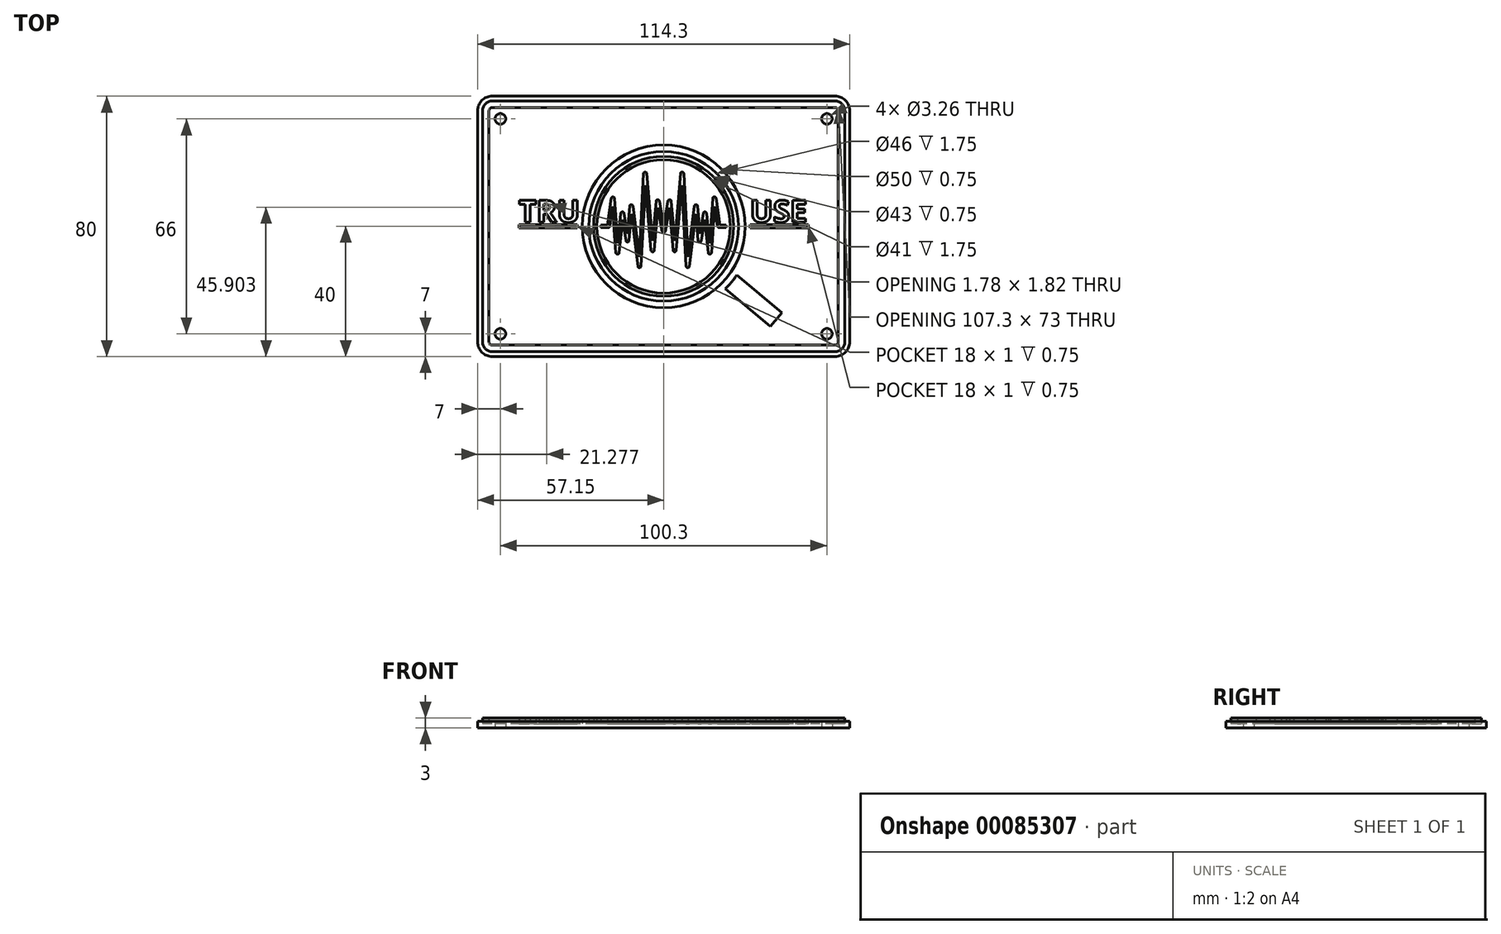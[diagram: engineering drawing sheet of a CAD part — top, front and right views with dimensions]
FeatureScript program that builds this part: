
annotation { "Feature Type Name" : "Feature", "Feature Type Description" : "" }
export const myFeature = defineFeature(function(context is Context, id is Id, definition is map)
    precondition{}
    {
        {
            var Q0;
            Q0=qCreatedBy(makeId("Front.planeOp"),FACE);
            var sketch = newSketch(context, id + "F0", { "sketchPlane" : qUnion([Q0])});
            skLineSegment(sketch, "E0.bottom", {"start": v(-57.15, 0) * mm, "end": v(57.15, 0) * mm});
            skLineSegment(sketch, "E0.top", {"start": v(-57.15, 2) * mm, "end": v(57.15, 2) * mm});
            skLineSegment(sketch, "E0.left", {"start": v(-57.15, 0) * mm, "end": v(-57.15, 2) * mm});
            skLineSegment(sketch, "E0.right", {"start": v(57.15, 0) * mm, "end": v(57.15, 2) * mm});
            skSolve(sketch);
        }
        {
            var Q0;
            Q0=makeQuery(id+"F0.imprint","IMPRINT",FACE,{"disambiguationData":[TD([[makeQuery(id+"F0.imprint","IMPRINT",EDGE,{"derivedFrom":sQuery(id+"F0.wireOp",EDGE,"E0.bottom")}),1.0]])]});
            extrude(context, id + "F1", {"entities" : qUnion([Q0]), "endBound" : BoundingType.SYMMETRIC, "depth" : 80 * mm});
        }
        {
            var Q0;
            Q0=qCreatedBy(makeId("Top.planeOp"),FACE);
            cPlane(context, id + "F2", {"entities" : qUnion([Q0]), "cplaneType" : CPlaneType.OFFSET, "offset" : 1.25 * mm, "width" : 150 * mm, "height" : 150 * mm});
        }
        {
            var Q0;
            Q0=qCreatedBy(id+"F2.planeOp",FACE);
            var sketch = newSketch(context, id + "F3", { "sketchPlane" : qUnion([Q0])});
            skCircle(sketch, "E1", {"center": v(0, 0) * mm, "radius": 25 * mm});
            skLineSegment(sketch, "E2.bottom", {"start": v(-44.5, -0.5) * mm, "end": v(-26.5, -0.5) * mm});
            skLineSegment(sketch, "E2.top", {"start": v(-44.5, 0.5) * mm, "end": v(-26.5, 0.5) * mm});
            skLineSegment(sketch, "E2.left", {"start": v(-44.5, -0.5) * mm, "end": v(-44.5, 0.5) * mm});
            skLineSegment(sketch, "E2.right", {"start": v(-26.5, -0.5) * mm, "end": v(-26.5, 0.5) * mm});
            skPoint(sketch, "E2.middle", {"position": v(-35.5, 0) * mm});
            skLineSegment(sketch, "E3.MirrorCS", {"start": v(44.5, 0.5) * mm, "end": v(26.5, 0.5) * mm});
            skLineSegment(sketch, "E4.MirrorCS", {"start": v(44.5, -0.5) * mm, "end": v(26.5, -0.5) * mm});
            skLineSegment(sketch, "E5.MirrorCS", {"start": v(26.5, -0.5) * mm, "end": v(26.5, 0.5) * mm});
            skLineSegment(sketch, "E6.MirrorCS", {"start": v(44.5, -0.5) * mm, "end": v(44.5, 0.5) * mm});
            skCircle(sketch, "E7", {"center": v(0, 0) * mm, "radius": 23 * mm});
            skSolve(sketch);
        }
        {
            var Q0;
            Q0 = qSketchRegion(id + "F3", true);
            extrude(context, id + "F4", {"entities" : qUnion([Q0]), "depth" : 1.75 * mm});
        }
        {
            var Q0;
            Q0=qCreatedBy(id+"F2.planeOp",FACE);
            var sketch = newSketch(context, id + "F5", { "sketchPlane" : qUnion([Q0])});
            skCircle(sketch, "E8", {"center": v(0, 0) * mm, "radius": 21.5 * mm});
            skCircle(sketch, "E9", {"center": v(0, 0) * mm, "radius": 20.5 * mm});
            skSolve(sketch);
        }
        {
            var Q0;
            Q0 = qSketchRegion(id + "F5", true);
            extrude(context, id + "F6", {"entities" : qUnion([Q0]), "depth" : 1.75 * mm});
        }
        {
            var Q0;
            Q0=qCreatedBy(id+"F2.planeOp",FACE);
            var sketch = newSketch(context, id + "F7", { "sketchPlane" : qUnion([Q0])});
            skLineSegment(sketch, "E10.0", {"start": v(19, -19.19) * mm, "end": v(32.78, -30.76) * mm});
            skLineSegment(sketch, "E11.0", {"start": v(22.49, -14.94) * mm, "end": v(36.32, -26.55) * mm});
            skLineSegment(sketch, "E12", {"start": v(36.32, -26.55) * mm, "end": v(32.78, -30.76) * mm});
            skArc(sketch, "E13", {"start": v(19, -19.19) * mm, "mid": v(20.85, -17.15) * mm, "end": v(22.49, -14.94) * mm});
            skSolve(sketch);
        }
        {
            var Q0;
            Q0 = qSketchRegion(id + "F7", true);
            extrude(context, id + "F8", {"entities" : qUnion([Q0]), "depth" : 1.75 * mm});
        }
        {
            var Q0;
            Q0=qCreatedBy(id+"F2.planeOp",FACE);
            var sketch = newSketch(context, id + "F9", { "sketchPlane" : qUnion([Q0])});
            skText(sketch, "E14", { "text": "TRU", "fontName": "OpenSans-Bold.ttf"});
            skText(sketch, "E15", { "text": "USE", "fontName": "OpenSans-Bold.ttf"});
            const initialGuessF9  = {"E14": [-0.0445, 0.00125, 1, 0, 0.00679], "E15": [0.0265, 0.00125, 1, 0, 0.00678]};
            skSetInitialGuess(sketch, initialGuessF9);
            skSolve(sketch);
        }
        {
            var Q0;
            Q0 = qSketchRegion(id + "F9", true);
            extrude(context, id + "F10", {"entities" : qUnion([Q0]), "depth" : 1.75 * mm});
        }
        {
            var Q0;
            Q0=qCreatedBy(id+"F2.planeOp",FACE);
            var sketch = newSketch(context, id + "F11", { "sketchPlane" : qUnion([Q0])});
            skPoint(sketch, "E16.middle", {"position": v(0, 0) * mm});
            skLineSegment(sketch, "E17.bottom", {"start": v(52.65, 38.5) * mm, "end": v(-52.65, 38.5) * mm});
            skLineSegment(sketch, "E17.top", {"start": v(52.65, -38.5) * mm, "end": v(-52.65, -38.5) * mm});
            skLineSegment(sketch, "E17.left", {"start": v(55.65, 35.5) * mm, "end": v(55.65, -35.5) * mm});
            skLineSegment(sketch, "E17.right", {"start": v(-55.65, 35.5) * mm, "end": v(-55.65, -35.5) * mm});
            skLineSegment(sketch, "E18.bottom", {"start": v(52.65, 36.5) * mm, "end": v(-52.65, 36.5) * mm});
            skLineSegment(sketch, "E18.top", {"start": v(52.65, -36.5) * mm, "end": v(-52.65, -36.5) * mm});
            skLineSegment(sketch, "E18.left", {"start": v(53.65, 35.5) * mm, "end": v(53.65, -35.5) * mm});
            skLineSegment(sketch, "E18.right", {"start": v(-53.65, 35.5) * mm, "end": v(-53.65, -35.5) * mm});
            skPoint(sketch, "E19.visualSharp", {"position": v(-55.65, 38.5) * mm});
            skArc(sketch, "E19.filletArc", {"start": v(-52.65, 38.5) * mm, "mid": v(-54.77, 37.62) * mm, "end": v(-55.65, 35.5) * mm});
            skPoint(sketch, "E20.visualSharp", {"position": v(55.65, 38.5) * mm});
            skArc(sketch, "E20.filletArc", {"start": v(55.65, 35.5) * mm, "mid": v(54.77, 37.62) * mm, "end": v(52.65, 38.5) * mm});
            skPoint(sketch, "E21.visualSharp", {"position": v(55.65, -38.5) * mm});
            skArc(sketch, "E21.filletArc", {"start": v(52.65, -38.5) * mm, "mid": v(54.77, -37.62) * mm, "end": v(55.65, -35.5) * mm});
            skPoint(sketch, "E22.visualSharp", {"position": v(-55.65, -38.5) * mm});
            skArc(sketch, "E22.filletArc", {"start": v(-55.65, -35.5) * mm, "mid": v(-54.77, -37.62) * mm, "end": v(-52.65, -38.5) * mm});
            skPoint(sketch, "E23.visualSharp", {"position": v(53.65, 36.5) * mm});
            skArc(sketch, "E23.filletArc", {"start": v(53.65, 35.5) * mm, "mid": v(53.36, 36.2) * mm, "end": v(52.65, 36.5) * mm});
            skPoint(sketch, "E24.visualSharp", {"position": v(-53.65, 36.5) * mm});
            skArc(sketch, "E24.filletArc", {"start": v(-52.65, 36.5) * mm, "mid": v(-53.36, 36.2) * mm, "end": v(-53.65, 35.5) * mm});
            skPoint(sketch, "E25.visualSharp", {"position": v(-53.65, -36.5) * mm});
            skArc(sketch, "E25.filletArc", {"start": v(-53.65, -35.5) * mm, "mid": v(-53.36, -36.2) * mm, "end": v(-52.65, -36.5) * mm});
            skPoint(sketch, "E26.visualSharp", {"position": v(53.65, -36.5) * mm});
            skArc(sketch, "E26.filletArc", {"start": v(52.65, -36.5) * mm, "mid": v(53.36, -36.2) * mm, "end": v(53.65, -35.5) * mm});
            skSolve(sketch);
        }
        {
            var Q0;
            Q0 = qSketchRegion(id + "F11", true);
            extrude(context, id + "F12", {"entities" : qUnion([Q0]), "depth" : 1.75 * mm});
        }
        {
            var Q0;
            Q0=qCreatedBy(id+"F2.planeOp",FACE);
            var sketch = newSketch(context, id + "F13", { "sketchPlane" : qUnion([Q0])});
            skLineSegment(sketch, "E27.bottom", {"start": v(-17.03, -0.38) * mm, "end": v(-19.25, -0.37) * mm});
            skLineSegment(sketch, "E27.top", {"start": v(-17.25, 0.38) * mm, "end": v(-19.25, 0.38) * mm});
            skLineSegment(sketch, "E27.right", {"start": v(-19.25, -0.37) * mm, "end": v(-19.25, 0.38) * mm});
            skPoint(sketch, "E27.middle", {"position": v(-18.25, 0) * mm});
            skLineSegment(sketch, "E28", {"start": v(-17.25, 0.37) * mm, "end": v(-16.09, 8.62) * mm});
            skLineSegment(sketch, "E29.0", {"start": v(-16.53, 0.06) * mm, "end": v(-15.68, 6.16) * mm});
            skPoint(sketch, "E27.left.start.orphan", {"position": v(-17.25, -0.38) * mm});
            skPoint(sketch, "E30.visualSharp", {"position": v(-16.6, -0.38) * mm});
            skArc(sketch, "E30.filletArc", {"start": v(-17.03, -0.38) * mm, "mid": v(-16.7, -0.25) * mm, "end": v(-16.53, 0.06) * mm});
            skLineSegment(sketch, "E31", {"start": v(-15.68, 6.16) * mm, "end": v(-14.68, -8.1) * mm});
            skLineSegment(sketch, "E32.0", {"start": v(-15.1, 8.58) * mm, "end": v(-14.13, -5.19) * mm});
            skPoint(sketch, "E33.visualSharp", {"position": v(-15.43, 13.33) * mm});
            skArc(sketch, "E33.filletArc", {"start": v(-15.1, 8.58) * mm, "mid": v(-15.58, 9.05) * mm, "end": v(-16.09, 8.62) * mm});
            skLineSegment(sketch, "E34", {"start": v(-14.13, -5.19) * mm, "end": v(-13.16, 4) * mm});
            skLineSegment(sketch, "E35.0", {"start": v(-13.68, -8.1) * mm, "end": v(-12.62, 2.03) * mm});
            skLineSegment(sketch, "E36", {"start": v(-12.62, 2.03) * mm, "end": v(-11.6, -4.4) * mm});
            skLineSegment(sketch, "E37.0", {"start": v(-12.17, 4.02) * mm, "end": v(-11.18, -2.27) * mm});
            skLineSegment(sketch, "E38", {"start": v(-11.18, -2.27) * mm, "end": v(-10.43, 6.22) * mm});
            skLineSegment(sketch, "E39.0", {"start": v(-10.6, -4.37) * mm, "end": v(-9.9, 3.78) * mm});
            skLineSegment(sketch, "E40", {"start": v(-9.9, 3.78) * mm, "end": v(-7.92, -12.26) * mm});
            skLineSegment(sketch, "E41.0", {"start": v(-9.44, 6.24) * mm, "end": v(-7.53, -9.33) * mm});
            skLineSegment(sketch, "E42", {"start": v(-7.53, -9.33) * mm, "end": v(-6.19, 16.22) * mm});
            skLineSegment(sketch, "E43.0", {"start": v(-6.93, -12.22) * mm, "end": v(-5.63, 12.61) * mm});
            skLineSegment(sketch, "E44", {"start": v(-5.63, 12.61) * mm, "end": v(-3.88, -7.38) * mm});
            skLineSegment(sketch, "E45.0", {"start": v(-5.2, 16.24) * mm, "end": v(-3.38, -4.47) * mm});
            skLineSegment(sketch, "E46", {"start": v(-3.38, -4.47) * mm, "end": v(-2.31, 7.74) * mm});
            skLineSegment(sketch, "E47.0", {"start": v(-2.88, -7.38) * mm, "end": v(-1.73, 5.74) * mm});
            skLineSegment(sketch, "E48", {"start": v(0, 12.7) * mm, "end": v(0, -16.33) * mm, "construction": true});
            skLineSegment(sketch, "E49", {"start": v(-1.73, 5.74) * mm, "end": v(-0.5, -1.53) * mm});
            skLineSegment(sketch, "E50.0", {"start": v(-1.32, 7.78) * mm, "end": v(0, 0.04) * mm});
            skPoint(sketch, "E51.visualSharp", {"position": v(-14.28, -13.8) * mm});
            skArc(sketch, "E51.filletArc", {"start": v(-14.68, -8.1) * mm, "mid": v(-14.19, -8.56) * mm, "end": v(-13.68, -8.1) * mm});
            skPoint(sketch, "E52.visualSharp", {"position": v(-12.77, 7.78) * mm});
            skArc(sketch, "E52.filletArc", {"start": v(-12.17, 4.02) * mm, "mid": v(-12.68, 4.45) * mm, "end": v(-13.16, 4) * mm});
            skPoint(sketch, "E53.visualSharp", {"position": v(-10.96, -8.42) * mm});
            skArc(sketch, "E53.filletArc", {"start": v(-11.6, -4.4) * mm, "mid": v(-11.09, -4.82) * mm, "end": v(-10.6, -4.37) * mm});
            skPoint(sketch, "E54.visualSharp", {"position": v(-10.02, 10.96) * mm});
            skArc(sketch, "E54.filletArc", {"start": v(-9.44, 6.24) * mm, "mid": v(-9.94, 6.67) * mm, "end": v(-10.43, 6.22) * mm});
            skPoint(sketch, "E55.visualSharp", {"position": v(-7.23, -17.93) * mm});
            skArc(sketch, "E55.filletArc", {"start": v(-7.92, -12.26) * mm, "mid": v(-7.4, -12.7) * mm, "end": v(-6.93, -12.22) * mm});
            skPoint(sketch, "E56.visualSharp", {"position": v(-5.81, 23.36) * mm});
            skArc(sketch, "E56.filletArc", {"start": v(-5.2, 16.24) * mm, "mid": v(-5.7, 16.7) * mm, "end": v(-6.19, 16.22) * mm});
            skPoint(sketch, "E57.visualSharp", {"position": v(-3.38, -13.07) * mm});
            skArc(sketch, "E57.filletArc", {"start": v(-3.88, -7.38) * mm, "mid": v(-3.38, -7.84) * mm, "end": v(-2.88, -7.38) * mm});
            skPoint(sketch, "E58.visualSharp", {"position": v(-1.97, 11.61) * mm});
            skArc(sketch, "E58.filletArc", {"start": v(-1.32, 7.78) * mm, "mid": v(-1.83, 8.2) * mm, "end": v(-2.31, 7.74) * mm});
            skArc(sketch, "E59.MirrorCS", {"start": v(17.03, -0.38) * mm, "mid": v(16.7, -0.25) * mm, "end": v(16.53, 0.06) * mm});
            skArc(sketch, "E60.MirrorCS", {"start": v(5.2, 16.24) * mm, "mid": v(5.7, 16.7) * mm, "end": v(6.19, 16.22) * mm});
            skArc(sketch, "E61.MirrorCS", {"start": v(1.32, 7.78) * mm, "mid": v(1.83, 8.2) * mm, "end": v(2.31, 7.74) * mm});
            skArc(sketch, "E62.MirrorCS", {"start": v(3.88, -7.38) * mm, "mid": v(3.38, -7.84) * mm, "end": v(2.88, -7.38) * mm});
            skArc(sketch, "E63.MirrorCS", {"start": v(14.68, -8.1) * mm, "mid": v(14.19, -8.56) * mm, "end": v(13.68, -8.1) * mm});
            skArc(sketch, "E64.MirrorCS", {"start": v(11.6, -4.4) * mm, "mid": v(11.09, -4.82) * mm, "end": v(10.6, -4.37) * mm});
            skArc(sketch, "E65.MirrorCS", {"start": v(9.44, 6.24) * mm, "mid": v(9.94, 6.67) * mm, "end": v(10.43, 6.22) * mm});
            skArc(sketch, "E66.MirrorCS", {"start": v(15.1, 8.58) * mm, "mid": v(15.58, 9.05) * mm, "end": v(16.09, 8.62) * mm});
            skArc(sketch, "E67.MirrorCS", {"start": v(12.17, 4.02) * mm, "mid": v(12.68, 4.45) * mm, "end": v(13.16, 4) * mm});
            skArc(sketch, "E68.MirrorCS", {"start": v(7.92, -12.26) * mm, "mid": v(7.4, -12.7) * mm, "end": v(6.93, -12.22) * mm});
            skLineSegment(sketch, "E69.MirrorCS", {"start": v(19.25, -0.37) * mm, "end": v(19.25, 0.38) * mm});
            skLineSegment(sketch, "E70.MirrorCS", {"start": v(17.03, -0.38) * mm, "end": v(19.25, -0.37) * mm});
            skPoint(sketch, "E71.MirrorP", {"position": v(16.6, -0.38) * mm});
            skLineSegment(sketch, "E72.MirrorCS", {"start": v(17.25, 0.38) * mm, "end": v(19.25, 0.38) * mm});
            skPoint(sketch, "E73.MirrorP", {"position": v(17.25, -0.38) * mm});
            skPoint(sketch, "E74.MirrorP", {"position": v(18.25, 0) * mm});
            skLineSegment(sketch, "E75.MirrorCS", {"start": v(7.53, -9.33) * mm, "end": v(6.19, 16.22) * mm});
            skPoint(sketch, "E76.MirrorP", {"position": v(12.77, 7.78) * mm});
            skLineSegment(sketch, "E77.MirrorCS", {"start": v(3.38, -4.47) * mm, "end": v(2.31, 7.74) * mm});
            skLineSegment(sketch, "E78.MirrorCS", {"start": v(12.17, 4.02) * mm, "end": v(11.18, -2.27) * mm});
            skLineSegment(sketch, "E79.MirrorCS", {"start": v(1.73, 5.74) * mm, "end": v(0.5, -1.53) * mm});
            skPoint(sketch, "E80.MirrorP", {"position": v(14.28, -13.8) * mm});
            skLineSegment(sketch, "E81.MirrorCS", {"start": v(1.32, 7.78) * mm, "end": v(0, 0.04) * mm});
            skLineSegment(sketch, "E82.MirrorCS", {"start": v(10.6, -4.37) * mm, "end": v(9.9, 3.78) * mm});
            skLineSegment(sketch, "E83.MirrorCS", {"start": v(9.9, 3.78) * mm, "end": v(7.92, -12.26) * mm});
            skPoint(sketch, "E84.MirrorP", {"position": v(10.96, -8.42) * mm});
            skLineSegment(sketch, "E85.MirrorCS", {"start": v(9.44, 6.24) * mm, "end": v(7.53, -9.33) * mm});
            skLineSegment(sketch, "E86.MirrorCS", {"start": v(2.88, -7.38) * mm, "end": v(1.73, 5.74) * mm});
            skLineSegment(sketch, "E87.MirrorCS", {"start": v(12.62, 2.03) * mm, "end": v(11.6, -4.4) * mm});
            skPoint(sketch, "E88.MirrorP", {"position": v(1.97, 11.61) * mm});
            skPoint(sketch, "E89.MirrorP", {"position": v(3.38, -13.07) * mm});
            skPoint(sketch, "E90.MirrorP", {"position": v(15.43, 13.33) * mm});
            skPoint(sketch, "E91.MirrorP", {"position": v(10.02, 10.96) * mm});
            skLineSegment(sketch, "E92.MirrorCS", {"start": v(5.2, 16.24) * mm, "end": v(3.38, -4.47) * mm});
            skLineSegment(sketch, "E93.MirrorCS", {"start": v(17.25, 0.37) * mm, "end": v(16.09, 8.62) * mm});
            skLineSegment(sketch, "E94.MirrorCS", {"start": v(5.63, 12.61) * mm, "end": v(3.88, -7.38) * mm});
            skLineSegment(sketch, "E95.MirrorCS", {"start": v(14.13, -5.19) * mm, "end": v(13.16, 4) * mm});
            skLineSegment(sketch, "E96.MirrorCS", {"start": v(13.68, -8.1) * mm, "end": v(12.62, 2.03) * mm});
            skLineSegment(sketch, "E97.MirrorCS", {"start": v(15.68, 6.16) * mm, "end": v(14.68, -8.1) * mm});
            skLineSegment(sketch, "E98.MirrorCS", {"start": v(6.93, -12.22) * mm, "end": v(5.63, 12.61) * mm});
            skLineSegment(sketch, "E99.MirrorCS", {"start": v(15.1, 8.58) * mm, "end": v(14.13, -5.19) * mm});
            skLineSegment(sketch, "E100.MirrorCS", {"start": v(16.53, 0.06) * mm, "end": v(15.68, 6.16) * mm});
            skLineSegment(sketch, "E101.MirrorCS", {"start": v(11.18, -2.27) * mm, "end": v(10.43, 6.22) * mm});
            skPoint(sketch, "E102.visualSharp", {"position": v(0, -4.42) * mm});
            skArc(sketch, "E102.filletArc", {"start": v(-0.5, -1.53) * mm, "mid": v(0, -1.95) * mm, "end": v(0.5, -1.53) * mm});
            skSolve(sketch);
        }
        {
            var Q0;
            Q0 = qSketchRegion(id + "F13", true);
            extrude(context, id + "F14", {"entities" : qUnion([Q0]), "depth" : 1.75 * mm});
        }
        {
            var Q0;
            Q0=makeQuery(id+"F1.opExtrude","CAP_EDGE",EDGE,{"disambiguationData":[OSD([sQuery(id+"F0.wireOp",EDGE,"E0.right")])],"isStart":true});
            var Q1;
            Q1=makeQuery(id+"F1.opExtrude","CAP_EDGE",EDGE,{"disambiguationData":[OSD([sQuery(id+"F0.wireOp",EDGE,"E0.right")])],"isStart":false});
            var Q2;
            Q2=makeQuery(id+"F1.opExtrude","CAP_EDGE",EDGE,{"disambiguationData":[OSD([sQuery(id+"F0.wireOp",EDGE,"E0.left")])],"isStart":false});
            var Q3;
            Q3=makeQuery(id+"F1.opExtrude","CAP_EDGE",EDGE,{"disambiguationData":[OSD([sQuery(id+"F0.wireOp",EDGE,"E0.left")])],"isStart":true});
            fillet(context, id + "F15", {"entities" : qUnion([Q0, Q1, Q2, Q3]), "radius" : 4.5 * mm, "tangentPropagation" : true, "allowEdgeOverflow" : false});
        }
        {
            var Q0;
            Q0=qCreatedBy(makeId("Top.planeOp"),FACE);
            var sketch = newSketch(context, id + "F16", { "sketchPlane" : qUnion([Q0])});
            skCircle(sketch, "E103", {"center": v(-50.15, 33) * mm, "radius": 1.63 * mm});
            skCircle(sketch, "E104.MirrorC", {"center": v(50.15, 33) * mm, "radius": 1.63 * mm});
            skCircle(sketch, "E105.MirrorC", {"center": v(-50.15, -33) * mm, "radius": 1.63 * mm});
            skCircle(sketch, "E106.MirrorC", {"center": v(50.15, -33) * mm, "radius": 1.63 * mm});
            skSolve(sketch);
        }
        {
            var Q0;
            Q0 = qSketchRegion(id + "F16", true);
            extrude(context, id + "F17", {"entities" : qUnion([Q0]), "operationType" : NewBodyOperationType.REMOVE, "endBound" : BoundingType.THROUGH_ALL, "depth" : 25 * mm});
        }
        {
            var Q0;
            Q0=makeQuery(id+"F14.opExtrude","SWEPT_BODY",BODY,{"disambiguationData":[OSD([sQuery(id+"F13.wireOp",EDGE,"E27.bottom"),sQuery(id+"F13.wireOp",EDGE,"E27.top"),sQuery(id+"F13.wireOp",EDGE,"E27.right"),sQuery(id+"F13.wireOp",EDGE,"E28"),sQuery(id+"F13.wireOp",EDGE,"E29.0"),sQuery(id+"F13.wireOp",EDGE,"E30.filletArc"),sQuery(id+"F13.wireOp",EDGE,"E31"),sQuery(id+"F13.wireOp",EDGE,"E32.0"),sQuery(id+"F13.wireOp",EDGE,"E33.filletArc"),sQuery(id+"F13.wireOp",EDGE,"E34"),sQuery(id+"F13.wireOp",EDGE,"E35.0"),sQuery(id+"F13.wireOp",EDGE,"E36"),sQuery(id+"F13.wireOp",EDGE,"E37.0"),sQuery(id+"F13.wireOp",EDGE,"E38"),sQuery(id+"F13.wireOp",EDGE,"E39.0"),sQuery(id+"F13.wireOp",EDGE,"E40"),sQuery(id+"F13.wireOp",EDGE,"E41.0"),sQuery(id+"F13.wireOp",EDGE,"E42"),sQuery(id+"F13.wireOp",EDGE,"E43.0"),sQuery(id+"F13.wireOp",EDGE,"E44"),sQuery(id+"F13.wireOp",EDGE,"E45.0"),sQuery(id+"F13.wireOp",EDGE,"E46"),sQuery(id+"F13.wireOp",EDGE,"E47.0"),sQuery(id+"F13.wireOp",EDGE,"E49"),sQuery(id+"F13.wireOp",EDGE,"E50.0"),sQuery(id+"F13.wireOp",EDGE,"E51.filletArc"),sQuery(id+"F13.wireOp",EDGE,"E52.filletArc"),sQuery(id+"F13.wireOp",EDGE,"E53.filletArc"),sQuery(id+"F13.wireOp",EDGE,"E54.filletArc"),sQuery(id+"F13.wireOp",EDGE,"E55.filletArc"),sQuery(id+"F13.wireOp",EDGE,"E56.filletArc"),sQuery(id+"F13.wireOp",EDGE,"E57.filletArc"),sQuery(id+"F13.wireOp",EDGE,"E58.filletArc"),sQuery(id+"F13.wireOp",EDGE,"E59.MirrorCS"),sQuery(id+"F13.wireOp",EDGE,"E60.MirrorCS"),sQuery(id+"F13.wireOp",EDGE,"E61.MirrorCS"),sQuery(id+"F13.wireOp",EDGE,"E62.MirrorCS"),sQuery(id+"F13.wireOp",EDGE,"E63.MirrorCS"),sQuery(id+"F13.wireOp",EDGE,"E64.MirrorCS"),sQuery(id+"F13.wireOp",EDGE,"E65.MirrorCS"),sQuery(id+"F13.wireOp",EDGE,"E66.MirrorCS"),sQuery(id+"F13.wireOp",EDGE,"E67.MirrorCS"),sQuery(id+"F13.wireOp",EDGE,"E68.MirrorCS"),sQuery(id+"F13.wireOp",EDGE,"E69.MirrorCS"),sQuery(id+"F13.wireOp",EDGE,"E70.MirrorCS"),sQuery(id+"F13.wireOp",EDGE,"E72.MirrorCS"),sQuery(id+"F13.wireOp",EDGE,"E75.MirrorCS"),sQuery(id+"F13.wireOp",EDGE,"E77.MirrorCS"),sQuery(id+"F13.wireOp",EDGE,"E78.MirrorCS"),sQuery(id+"F13.wireOp",EDGE,"E79.MirrorCS"),sQuery(id+"F13.wireOp",EDGE,"E81.MirrorCS"),sQuery(id+"F13.wireOp",EDGE,"E82.MirrorCS"),sQuery(id+"F13.wireOp",EDGE,"E83.MirrorCS"),sQuery(id+"F13.wireOp",EDGE,"E85.MirrorCS"),sQuery(id+"F13.wireOp",EDGE,"E86.MirrorCS"),sQuery(id+"F13.wireOp",EDGE,"E87.MirrorCS"),sQuery(id+"F13.wireOp",EDGE,"E92.MirrorCS"),sQuery(id+"F13.wireOp",EDGE,"E93.MirrorCS"),sQuery(id+"F13.wireOp",EDGE,"E94.MirrorCS"),sQuery(id+"F13.wireOp",EDGE,"E95.MirrorCS"),sQuery(id+"F13.wireOp",EDGE,"E96.MirrorCS"),sQuery(id+"F13.wireOp",EDGE,"E97.MirrorCS"),sQuery(id+"F13.wireOp",EDGE,"E98.MirrorCS"),sQuery(id+"F13.wireOp",EDGE,"E99.MirrorCS"),sQuery(id+"F13.wireOp",EDGE,"E100.MirrorCS"),sQuery(id+"F13.wireOp",EDGE,"E101.MirrorCS"),sQuery(id+"F13.wireOp",EDGE,"E102.filletArc")])]});
            var Q1;
            Q1=makeQuery(id+"F1.opExtrude","SWEPT_BODY",BODY,{"disambiguationData":[OSD([sQuery(id+"F0.wireOp",EDGE,"E0.bottom"),sQuery(id+"F0.wireOp",EDGE,"E0.top"),sQuery(id+"F0.wireOp",EDGE,"E0.left"),sQuery(id+"F0.wireOp",EDGE,"E0.right")])]});
            booleanBodies(context, id + "F18", {"operationType" : BooleanOperationType.SUBTRACTION, "tools" : qUnion([Q0]), "targets" : qUnion([Q1]), "keepTools" : true});
        }
        {
            var Q0;
            Q0=makeQuery(id+"F4.opExtrude","SWEPT_BODY",BODY,{"disambiguationData":[OSD([sQuery(id+"F3.wireOp",EDGE,"E1"),sQuery(id+"F3.wireOp",EDGE,"E7")])]});
            var Q1;
            Q1=makeQuery(id+"F4.opExtrude","SWEPT_BODY",BODY,{"disambiguationData":[OSD([sQuery(id+"F3.wireOp",EDGE,"E2.bottom"),sQuery(id+"F3.wireOp",EDGE,"E2.top"),sQuery(id+"F3.wireOp",EDGE,"E2.left"),sQuery(id+"F3.wireOp",EDGE,"E2.right")])]});
            var Q2;
            Q2=makeQuery(id+"F4.opExtrude","SWEPT_BODY",BODY,{"disambiguationData":[OSD([sQuery(id+"F3.wireOp",EDGE,"E3.MirrorCS"),sQuery(id+"F3.wireOp",EDGE,"E4.MirrorCS"),sQuery(id+"F3.wireOp",EDGE,"E5.MirrorCS"),sQuery(id+"F3.wireOp",EDGE,"E6.MirrorCS")])]});
            var Q3;
            Q3=makeQuery(id+"F1.opExtrude","SWEPT_BODY",BODY,{"disambiguationData":[OSD([sQuery(id+"F0.wireOp",EDGE,"E0.bottom"),sQuery(id+"F0.wireOp",EDGE,"E0.top"),sQuery(id+"F0.wireOp",EDGE,"E0.left"),sQuery(id+"F0.wireOp",EDGE,"E0.right")])]});
            booleanBodies(context, id + "F19", {"operationType" : BooleanOperationType.SUBTRACTION, "tools" : qUnion([Q0, Q1, Q2]), "targets" : qUnion([Q3]), "keepTools" : true});
        }
        {
            var Q0;
            Q0=makeQuery(id+"F6.opExtrude","SWEPT_BODY",BODY,{"disambiguationData":[OSD([sQuery(id+"F5.wireOp",EDGE,"E8"),sQuery(id+"F5.wireOp",EDGE,"E9")])]});
            var Q1;
            Q1=makeQuery(id+"F1.opExtrude","SWEPT_BODY",BODY,{"disambiguationData":[OSD([sQuery(id+"F0.wireOp",EDGE,"E0.bottom"),sQuery(id+"F0.wireOp",EDGE,"E0.top"),sQuery(id+"F0.wireOp",EDGE,"E0.left"),sQuery(id+"F0.wireOp",EDGE,"E0.right")])]});
            booleanBodies(context, id + "F20", {"operationType" : BooleanOperationType.SUBTRACTION, "tools" : qUnion([Q0]), "targets" : qUnion([Q1]), "keepTools" : true});
        }
        {
            var Q0;
            Q0=makeQuery(id+"F8.opExtrude","SWEPT_BODY",BODY,{"disambiguationData":[OSD([sQuery(id+"F7.wireOp",EDGE,"E10.0"),sQuery(id+"F7.wireOp",EDGE,"E11.0"),sQuery(id+"F7.wireOp",EDGE,"E12"),sQuery(id+"F7.wireOp",EDGE,"E13")])]});
            var Q1;
            Q1=makeQuery(id+"F1.opExtrude","SWEPT_BODY",BODY,{"disambiguationData":[OSD([sQuery(id+"F0.wireOp",EDGE,"E0.bottom"),sQuery(id+"F0.wireOp",EDGE,"E0.top"),sQuery(id+"F0.wireOp",EDGE,"E0.left"),sQuery(id+"F0.wireOp",EDGE,"E0.right")])]});
            booleanBodies(context, id + "F21", {"operationType" : BooleanOperationType.SUBTRACTION, "tools" : qUnion([Q0]), "targets" : qUnion([Q1]), "keepTools" : true});
        }
        {
            var Q0;
            Q0=makeQuery(id+"F10.opExtrude","SWEPT_BODY",BODY,{"disambiguationData":[OSD([sQuery(id+"F9.wireOp",EDGE,"E14.sketch_text.stroke-0"),sQuery(id+"F9.wireOp",EDGE,"E14.sketch_text.stroke-1"),sQuery(id+"F9.wireOp",EDGE,"E14.sketch_text.stroke-2"),sQuery(id+"F9.wireOp",EDGE,"E14.sketch_text.stroke-3"),sQuery(id+"F9.wireOp",EDGE,"E14.sketch_text.stroke-4"),sQuery(id+"F9.wireOp",EDGE,"E14.sketch_text.stroke-5"),sQuery(id+"F9.wireOp",EDGE,"E14.sketch_text.stroke-6"),sQuery(id+"F9.wireOp",EDGE,"E14.sketch_text.stroke-7")])]});
            var Q1;
            Q1=makeQuery(id+"F10.opExtrude","SWEPT_BODY",BODY,{"disambiguationData":[OSD([sQuery(id+"F9.wireOp",EDGE,"E14.sketch_text.stroke-8"),sQuery(id+"F9.wireOp",EDGE,"E14.sketch_text.stroke-9"),sQuery(id+"F9.wireOp",EDGE,"E14.sketch_text.stroke-10"),sQuery(id+"F9.wireOp",EDGE,"E14.sketch_text.stroke-11"),sQuery(id+"F9.wireOp",EDGE,"E14.sketch_text.stroke-12"),sQuery(id+"F9.wireOp",EDGE,"E14.sketch_text.stroke-13"),sQuery(id+"F9.wireOp",EDGE,"E14.sketch_text.stroke-14"),sQuery(id+"F9.wireOp",EDGE,"E14.sketch_text.stroke-15"),sQuery(id+"F9.wireOp",EDGE,"E14.sketch_text.stroke-16"),sQuery(id+"F9.wireOp",EDGE,"E14.sketch_text.stroke-17"),sQuery(id+"F9.wireOp",EDGE,"E14.sketch_text.stroke-18"),sQuery(id+"F9.wireOp",EDGE,"E14.sketch_text.stroke-19"),sQuery(id+"F9.wireOp",EDGE,"E14.sketch_text.stroke-20"),sQuery(id+"F9.wireOp",EDGE,"E14.sketch_text.stroke-21"),sQuery(id+"F9.wireOp",EDGE,"E14.sketch_text.stroke-22"),sQuery(id+"F9.wireOp",EDGE,"E14.sketch_text.stroke-23"),sQuery(id+"F9.wireOp",EDGE,"E14.sketch_text.stroke-24"),sQuery(id+"F9.wireOp",EDGE,"E14.sketch_text.stroke-25"),sQuery(id+"F9.wireOp",EDGE,"E14.sketch_text.stroke-26")])]});
            var Q2;
            Q2=makeQuery(id+"F10.opExtrude","SWEPT_BODY",BODY,{"disambiguationData":[OSD([sQuery(id+"F9.wireOp",EDGE,"E14.sketch_text.stroke-27"),sQuery(id+"F9.wireOp",EDGE,"E14.sketch_text.stroke-28"),sQuery(id+"F9.wireOp",EDGE,"E14.sketch_text.stroke-29"),sQuery(id+"F9.wireOp",EDGE,"E14.sketch_text.stroke-30"),sQuery(id+"F9.wireOp",EDGE,"E14.sketch_text.stroke-31"),sQuery(id+"F9.wireOp",EDGE,"E14.sketch_text.stroke-32"),sQuery(id+"F9.wireOp",EDGE,"E14.sketch_text.stroke-33"),sQuery(id+"F9.wireOp",EDGE,"E14.sketch_text.stroke-34"),sQuery(id+"F9.wireOp",EDGE,"E14.sketch_text.stroke-35"),sQuery(id+"F9.wireOp",EDGE,"E14.sketch_text.stroke-36"),sQuery(id+"F9.wireOp",EDGE,"E14.sketch_text.stroke-37"),sQuery(id+"F9.wireOp",EDGE,"E14.sketch_text.stroke-38"),sQuery(id+"F9.wireOp",EDGE,"E14.sketch_text.stroke-39"),sQuery(id+"F9.wireOp",EDGE,"E14.sketch_text.stroke-40"),sQuery(id+"F9.wireOp",EDGE,"E14.sketch_text.stroke-41")])]});
            var Q3;
            Q3=makeQuery(id+"F10.opExtrude","SWEPT_BODY",BODY,{"disambiguationData":[OSD([sQuery(id+"F9.wireOp",EDGE,"E15.sketch_text.stroke-0"),sQuery(id+"F9.wireOp",EDGE,"E15.sketch_text.stroke-1"),sQuery(id+"F9.wireOp",EDGE,"E15.sketch_text.stroke-2"),sQuery(id+"F9.wireOp",EDGE,"E15.sketch_text.stroke-3"),sQuery(id+"F9.wireOp",EDGE,"E15.sketch_text.stroke-4"),sQuery(id+"F9.wireOp",EDGE,"E15.sketch_text.stroke-5"),sQuery(id+"F9.wireOp",EDGE,"E15.sketch_text.stroke-6"),sQuery(id+"F9.wireOp",EDGE,"E15.sketch_text.stroke-7"),sQuery(id+"F9.wireOp",EDGE,"E15.sketch_text.stroke-8"),sQuery(id+"F9.wireOp",EDGE,"E15.sketch_text.stroke-9"),sQuery(id+"F9.wireOp",EDGE,"E15.sketch_text.stroke-10"),sQuery(id+"F9.wireOp",EDGE,"E15.sketch_text.stroke-11"),sQuery(id+"F9.wireOp",EDGE,"E15.sketch_text.stroke-12"),sQuery(id+"F9.wireOp",EDGE,"E15.sketch_text.stroke-13"),sQuery(id+"F9.wireOp",EDGE,"E15.sketch_text.stroke-14")])]});
            var Q4;
            Q4=makeQuery(id+"F10.opExtrude","SWEPT_BODY",BODY,{"disambiguationData":[OSD([sQuery(id+"F9.wireOp",EDGE,"E15.sketch_text.stroke-15"),sQuery(id+"F9.wireOp",EDGE,"E15.sketch_text.stroke-16"),sQuery(id+"F9.wireOp",EDGE,"E15.sketch_text.stroke-17"),sQuery(id+"F9.wireOp",EDGE,"E15.sketch_text.stroke-18"),sQuery(id+"F9.wireOp",EDGE,"E15.sketch_text.stroke-19"),sQuery(id+"F9.wireOp",EDGE,"E15.sketch_text.stroke-20"),sQuery(id+"F9.wireOp",EDGE,"E15.sketch_text.stroke-21"),sQuery(id+"F9.wireOp",EDGE,"E15.sketch_text.stroke-22"),sQuery(id+"F9.wireOp",EDGE,"E15.sketch_text.stroke-23"),sQuery(id+"F9.wireOp",EDGE,"E15.sketch_text.stroke-24"),sQuery(id+"F9.wireOp",EDGE,"E15.sketch_text.stroke-25"),sQuery(id+"F9.wireOp",EDGE,"E15.sketch_text.stroke-26"),sQuery(id+"F9.wireOp",EDGE,"E15.sketch_text.stroke-27"),sQuery(id+"F9.wireOp",EDGE,"E15.sketch_text.stroke-28"),sQuery(id+"F9.wireOp",EDGE,"E15.sketch_text.stroke-29"),sQuery(id+"F9.wireOp",EDGE,"E15.sketch_text.stroke-30"),sQuery(id+"F9.wireOp",EDGE,"E15.sketch_text.stroke-31"),sQuery(id+"F9.wireOp",EDGE,"E15.sketch_text.stroke-32"),sQuery(id+"F9.wireOp",EDGE,"E15.sketch_text.stroke-33"),sQuery(id+"F9.wireOp",EDGE,"E15.sketch_text.stroke-34"),sQuery(id+"F9.wireOp",EDGE,"E15.sketch_text.stroke-35"),sQuery(id+"F9.wireOp",EDGE,"E15.sketch_text.stroke-36"),sQuery(id+"F9.wireOp",EDGE,"E15.sketch_text.stroke-37"),sQuery(id+"F9.wireOp",EDGE,"E15.sketch_text.stroke-38"),sQuery(id+"F9.wireOp",EDGE,"E15.sketch_text.stroke-39"),sQuery(id+"F9.wireOp",EDGE,"E15.sketch_text.stroke-40"),sQuery(id+"F9.wireOp",EDGE,"E15.sketch_text.stroke-41"),sQuery(id+"F9.wireOp",EDGE,"E15.sketch_text.stroke-42")])]});
            var Q5;
            Q5=makeQuery(id+"F10.opExtrude","SWEPT_BODY",BODY,{"disambiguationData":[OSD([sQuery(id+"F9.wireOp",EDGE,"E15.sketch_text.stroke-43"),sQuery(id+"F9.wireOp",EDGE,"E15.sketch_text.stroke-44"),sQuery(id+"F9.wireOp",EDGE,"E15.sketch_text.stroke-45"),sQuery(id+"F9.wireOp",EDGE,"E15.sketch_text.stroke-46"),sQuery(id+"F9.wireOp",EDGE,"E15.sketch_text.stroke-47"),sQuery(id+"F9.wireOp",EDGE,"E15.sketch_text.stroke-48"),sQuery(id+"F9.wireOp",EDGE,"E15.sketch_text.stroke-49"),sQuery(id+"F9.wireOp",EDGE,"E15.sketch_text.stroke-50"),sQuery(id+"F9.wireOp",EDGE,"E15.sketch_text.stroke-51"),sQuery(id+"F9.wireOp",EDGE,"E15.sketch_text.stroke-52"),sQuery(id+"F9.wireOp",EDGE,"E15.sketch_text.stroke-53"),sQuery(id+"F9.wireOp",EDGE,"E15.sketch_text.stroke-54")])]});
            var Q6;
            Q6=makeQuery(id+"F1.opExtrude","SWEPT_BODY",BODY,{"disambiguationData":[OSD([sQuery(id+"F0.wireOp",EDGE,"E0.bottom"),sQuery(id+"F0.wireOp",EDGE,"E0.top"),sQuery(id+"F0.wireOp",EDGE,"E0.left"),sQuery(id+"F0.wireOp",EDGE,"E0.right")])]});
            booleanBodies(context, id + "F22", {"operationType" : BooleanOperationType.SUBTRACTION, "tools" : qUnion([Q0, Q1, Q2, Q3, Q4, Q5]), "targets" : qUnion([Q6]), "keepTools" : true});
        }
        {
            var Q0;
            Q0=makeQuery(id+"F12.opExtrude","SWEPT_BODY",BODY,{"disambiguationData":[OSD([sQuery(id+"F11.wireOp",EDGE,"E17.bottom"),sQuery(id+"F11.wireOp",EDGE,"E17.top"),sQuery(id+"F11.wireOp",EDGE,"E17.left"),sQuery(id+"F11.wireOp",EDGE,"E17.right"),sQuery(id+"F11.wireOp",EDGE,"E18.bottom"),sQuery(id+"F11.wireOp",EDGE,"E18.top"),sQuery(id+"F11.wireOp",EDGE,"E18.left"),sQuery(id+"F11.wireOp",EDGE,"E18.right"),sQuery(id+"F11.wireOp",EDGE,"E19.filletArc"),sQuery(id+"F11.wireOp",EDGE,"E20.filletArc"),sQuery(id+"F11.wireOp",EDGE,"E21.filletArc"),sQuery(id+"F11.wireOp",EDGE,"E22.filletArc"),sQuery(id+"F11.wireOp",EDGE,"E23.filletArc"),sQuery(id+"F11.wireOp",EDGE,"E24.filletArc"),sQuery(id+"F11.wireOp",EDGE,"E25.filletArc"),sQuery(id+"F11.wireOp",EDGE,"E26.filletArc")])]});
            var Q1;
            Q1=makeQuery(id+"F1.opExtrude","SWEPT_BODY",BODY,{"disambiguationData":[OSD([sQuery(id+"F0.wireOp",EDGE,"E0.bottom"),sQuery(id+"F0.wireOp",EDGE,"E0.top"),sQuery(id+"F0.wireOp",EDGE,"E0.left"),sQuery(id+"F0.wireOp",EDGE,"E0.right")])]});
            booleanBodies(context, id + "F23", {"operationType" : BooleanOperationType.SUBTRACTION, "tools" : qUnion([Q0]), "targets" : qUnion([Q1]), "keepTools" : true});
        }
    });
